# Revit family: Gira_126567
name_source: partatom
category: Electrical Fixtures
revit_build: Autodesk Revit 2017 (Build: 20160225_1515(x64)
units: mm (PartAtom-declared; Revit-internal decimal feet)

## family parameters
Cut with Voids When Loaded = No
Host = Face
Maintain Annotation Orientation = Yes
Part Type = Normal
Room Calculation Point = No
Round Connector Dimension = Use Diameter
Shared = No

## types (1)
- Farbkamera Türstation Gira TX_44 (WG UP) Anthrazit
    Available = Yes
    BIM (1) = https://media.live.bim.site
    Category = Externe Kamera für Türkommunikation
    Data sheet (1) = https://katalog.gira.de
    Default Elevation = 1219 mm
    Description = Farbkamera für Türstation  Anthrazit Merkmale: - Montage in eine handelsübliche Unterputz-Gerätedose. - Passend in die Abdeckrahmen des Schalterprogramms Gira TX_44. - Modularer Aufbau, somit einfache Montage und Erweiterbarkeit. - Signalübertragung und Versorgung der Audio- und Videokomponenten über verpolungssicheren und kurzschlussfesten 2-Draht-Bus. - Erweiterung der Türstationen um eine Farbkamera mit automatischer Tag- bzw. Nachtumschaltung. - Leuchtdioden sorgen im Nachtbetrieb für eine gleichmäßige Gesichtsfeldausleuchtung im Nahbereich. - Kamera horizontal und vertikal um 20 manuell schwenkbar. In Kombination mit dem Weitwinkelobjektiv ergibt sich daraus ein sehr großer Sichtwinkel im Türeingangsbereich. - Automatische Gegenlichtkompensation. - Automatischer Weißabgleich. - Automatische Verstärkungsregelung (AGC). - Integrierte temperaturabhängige Kameraheizung. - Spritzwasserdichte Abdeckung. - Kameraabdeckung aus schlagfestem Kunststoff, bei Beschädigung, z. B. durch Vandalismus, leicht austauschbar.  Hinweise : - Die Farbkamera darf nicht direkt unter einer Leuchte angeordnet werden. - Geeignet zum Einsatz in Gira Energiesäule. - Nicht geeignet zum Einsatz in Gira Energiesäule mit Licht.
    Farbe = anthrazit
    GTIN = 4010337265672
    HAN = 126567
    HeinzeBIM = https://bimportal.heinze.de
    Installationstechnik = Bus-System
    Kategorie = Externe Kamera für Türkommunikation
    Keynote = TX44_Komplettgerät_Kamera
    Manufacturer = Gira
    Manufacturer URL = https://www.gira.de
    Montageart = Einbau
    Name = Farbkamera Türstation Gira TX_44 (WG UP) Anthrazit
    Region = DE
    URL = http://katalog.gira.de
    Verfügbar = Ja
    Werkstoff = sonstige

## geometry (parser evidence)
native form markers: Blend x4, Sweep x2
no freeform markers — native parametric forms only
